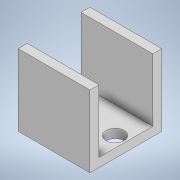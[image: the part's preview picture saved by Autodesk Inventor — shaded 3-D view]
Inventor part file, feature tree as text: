
AUTODESK INVENTOR PART (.ipt)
format: ipt  version: 2021 (Build 250183000, 183)  size: 114,688 bytes
history: native  units: in
note: dims shown in document units (in); Inventor stores cm internally (conversion verified against a paired STEP export)
features: extrude x2, sketch x2, mirror x1, projected_geometry x1
ambient origin geometry x8: Origin, YZ Plane, XZ Plane, XY Plane, X Axis, Y Axis, Z Axis, Center Point
bodies: Solid1 (feature_tree)
feature tree (6):
  extrude  "Extrusion1"  Depth=0.5in
  extrude  "Extrusion2"  Depth=0.375in
  mirror  "Mirror1"
  sketch  "Sketch2"  dims[d0=0.5in d1=0.5in]
  sketch  "Sketch3"  dims[d2=0.375in d3=0.375in d4=0.5in d5=0.0in d6=0.125in d7=0.175in d8=0.0in d9=0.0in]
  projected_geometry  "Projected Loop1"
